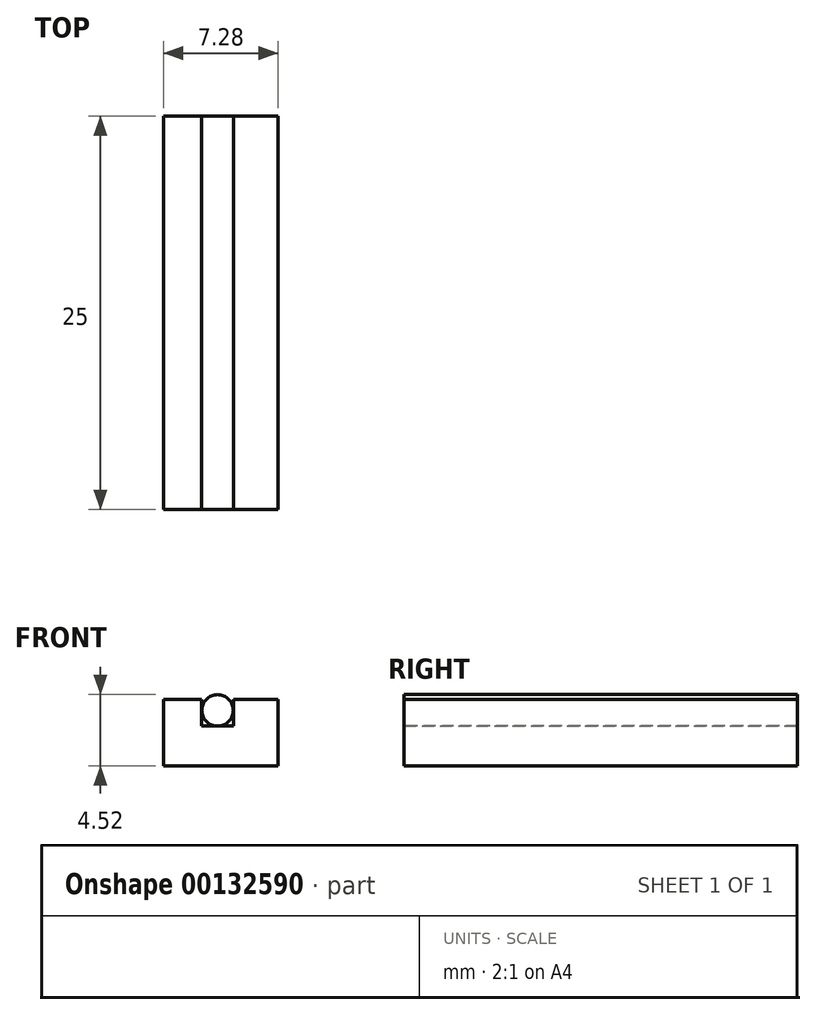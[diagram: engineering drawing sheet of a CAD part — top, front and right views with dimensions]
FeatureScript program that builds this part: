
annotation { "Feature Type Name" : "Feature", "Feature Type Description" : "" }
export const myFeature = defineFeature(function(context is Context, id is Id, definition is map)
    precondition{}
    {
        {
            var Q0;
            Q0=qCreatedBy(makeId("Front.planeOp"),FACE);
            var sketch = newSketch(context, id + "F0", { "sketchPlane" : qUnion([Q0])});
            skCircle(sketch, "E0", {"center": v(0, 0) * mm, "radius": 1 * mm});
            skSolve(sketch);
        }
        {
            var Q0;
            Q0 = qSketchRegion(id + "F0", true);
            extrude(context, id + "F1", {"entities" : qUnion([Q0]), "depth" : 25 * mm, "offsetDistance" : 25 * mm});
        }
        {
            var Q0;
            Q0=makeQuery(id+"F1.opExtrude","CAP_FACE",FACE,{"disambiguationData":[OSD([sQuery(id+"F0.wireOp",EDGE,"E0")])],"isStart":false});
            var sketch = newSketch(context, id + "F2", { "sketchPlane" : qUnion([Q0])});
            skLineSegment(sketch, "E1", {"start": v(-1, 0.7) * mm, "end": v(-1, -1) * mm});
            skLineSegment(sketch, "E2", {"start": v(-1, -1) * mm, "end": v(1, -1) * mm});
            skLineSegment(sketch, "E3", {"start": v(1, -1) * mm, "end": v(1, 0.7) * mm});
            skLineSegment(sketch, "E4", {"start": v(1, 0.7) * mm, "end": v(3.84, 0.7) * mm});
            skLineSegment(sketch, "E5", {"start": v(3.84, 0.7) * mm, "end": v(3.84, -3.52) * mm});
            skLineSegment(sketch, "E6", {"start": v(3.84, -3.52) * mm, "end": v(-3.44, -3.52) * mm});
            skLineSegment(sketch, "E7", {"start": v(-3.44, -3.52) * mm, "end": v(-3.44, 0.7) * mm});
            skLineSegment(sketch, "E8", {"start": v(-3.44, 0.7) * mm, "end": v(-1, 0.7) * mm});
            skSolve(sketch);
        }
        {
            var Q0;
            {var subQ0=sQuery(id+"F2.wireOp",EDGE,"E4");Q0=makeQuery(id+"F2.imprint","IMPRINT",FACE,{"disambiguationData":[TD([[makeQuery(id+"F2.imprint","IMPRINT",EDGE,{"derivedFrom":subQ0}),-1.0]])]});}
            extrude(context, id + "F3", {"entities" : qUnion([Q0]), "oppositeDirection" : true, "depth" : 25 * mm, "offsetDistance" : 25 * mm});
        }
    });
